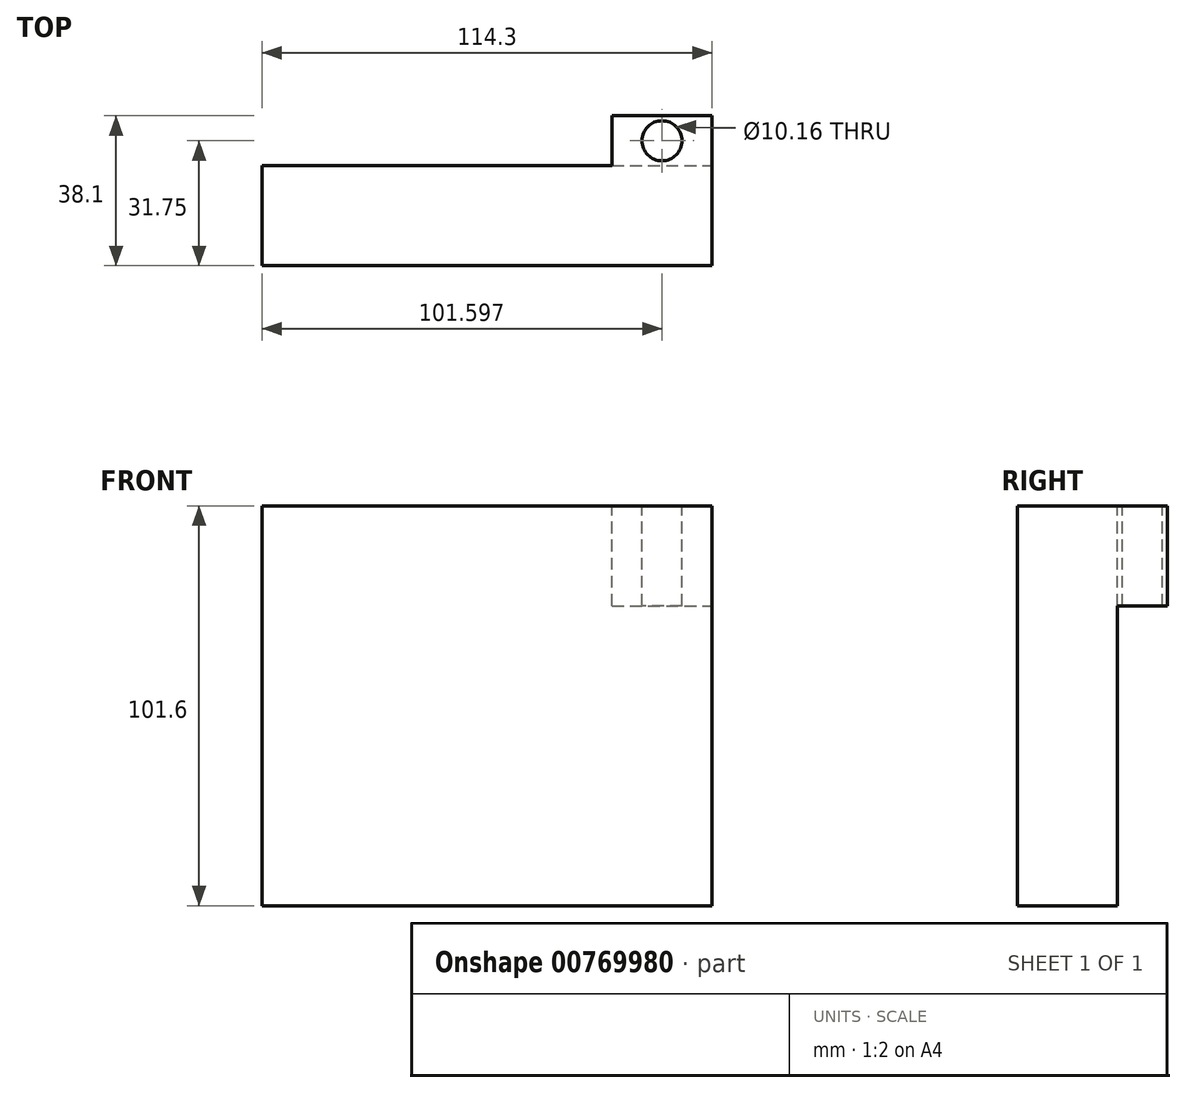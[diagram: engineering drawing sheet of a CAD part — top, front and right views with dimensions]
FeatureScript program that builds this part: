
annotation { "Feature Type Name" : "Feature", "Feature Type Description" : "" }
export const myFeature = defineFeature(function(context is Context, id is Id, definition is map)
    precondition{}
    {
        {
            var Q0;
            Q0=qCreatedBy(makeId("Front.planeOp"),FACE);
            var sketch = newSketch(context, id + "F0", { "sketchPlane" : qUnion([Q0])});
            skLineSegment(sketch, "E0.bottom", {"start": v(-101.4, 95.41) * mm, "end": v(12.9, 95.41) * mm});
            skLineSegment(sketch, "E0.top", {"start": v(-101.4, -6.19) * mm, "end": v(12.9, -6.19) * mm});
            skLineSegment(sketch, "E0.left", {"start": v(-101.4, 95.41) * mm, "end": v(-101.4, -6.19) * mm});
            skLineSegment(sketch, "E0.right", {"start": v(12.9, 95.41) * mm, "end": v(12.9, -6.19) * mm});
            skSolve(sketch);
        }
        {
            var Q0;
            Q0 = qSketchRegion(id + "F0", true);
            extrude(context, id + "F1", {"entities" : qUnion([Q0]), "depth" : 25.4 * mm, "offsetDistance" : 25.4 * mm});
        }
        {
            var Q0;
            {var subQ0=sQuery(id+"F0.wireOp",EDGE,"E0.bottom");Q0=makeQuery(id+"FLVJZS1soLFqfxB_1.boolean.opBoolean","MERGE",FACE,{"derivedFrom":[makeQuery(id+"F2oU1E1NIX52K6T_1.boolean.opBoolean","MERGE",FACE,{"derivedFrom":[makeQuery(id+"F1.opExtrude","SWEPT_FACE",FACE,{"disambiguationData":[OSD([subQ0])]}),makeQuery(id+"F2oU1E1NIX52K6T_1.opExtrude","SWEPT_FACE",FACE,{"disambiguationData":[OSD([subQ0,sQuery(id+"F0.wireOp",EDGE,"E0.left")])]})]}),makeQuery(id+"FLVJZS1soLFqfxB_1.opExtrude","SWEPT_FACE",FACE,{"disambiguationData":[OSD([subQ0,sQuery(id+"F0.wireOp",EDGE,"E0.right")])]})]});}
            var sketch = newSketch(context, id + "F2", { "sketchPlane" : qUnion([Q0])});
            skLineSegment(sketch, "E1.bottom", {"start": v(-12.5, 0) * mm, "end": v(12.9, 0) * mm});
            skLineSegment(sketch, "E1.top", {"start": v(-12.5, 12.7) * mm, "end": v(12.9, 12.7) * mm});
            skLineSegment(sketch, "E1.left", {"start": v(-12.5, 0) * mm, "end": v(-12.5, 12.7) * mm});
            skLineSegment(sketch, "E1.right", {"start": v(12.9, 0) * mm, "end": v(12.9, 12.7) * mm});
            skPoint(sketch, "E2", {"position": v(-44.24, 6.35) * mm});
            skPoint(sketch, "E2.positionSnap0", {"position": v(-44.24, 0) * mm});
            skPoint(sketch, "E2.positionSnap1", {"position": v(12.9, 6.35) * mm});
            skSolve(sketch);
        }
        {
            var Q0;
            Q0=makeQuery(id+"F2.imprint","IMPRINT",FACE,{"disambiguationData":[TD([[makeQuery(id+"F2.imprint","IMPRINT",EDGE,{"derivedFrom":sQuery(id+"F2.wireOp",EDGE,"E1.bottom")}),1.0]])]});
            extrude(context, id + "F3", {"entities" : qUnion([Q0]), "oppositeDirection" : true, "depth" : 25.4 * mm, "offsetDistance" : 25.4 * mm});
        }
        {
            var Q0;
            Q0=sQuery(id+"F2.wireOp",VERTEX,"E2");
            var Q1;
            Q1=makeQuery(id+"F3.opExtrude","SWEPT_BODY",BODY,{"disambiguationData":[OSD([sQuery(id+"F2.wireOp",EDGE,"E1.bottom"),sQuery(id+"F2.wireOp",EDGE,"E1.top"),sQuery(id+"F2.wireOp",EDGE,"E1.left"),sQuery(id+"F2.wireOp",EDGE,"E1.right")])]});
            hole(context, id + "F4", {"style" : HoleStyle.SIMPLE, "endStyle" : HoleEndStyle.THROUGH, "holeDiameter" : 10.16 * mm, "majorDiameter" : 6.35 * mm, "isTappedThrough" : true, "tappedDepth" : 12.7 * mm, "tapClearance" : 3, "locations" : qUnion([Q0]), "scope" : qUnion([Q1])});
        }
        {
            var Q0;
            Q0=makeQuery(id+"F3.opExtrude","SWEPT_BODY",BODY,{"disambiguationData":[OSD([sQuery(id+"F2.wireOp",EDGE,"E1.bottom"),sQuery(id+"F2.wireOp",EDGE,"E1.top"),sQuery(id+"F2.wireOp",EDGE,"E1.left"),sQuery(id+"F2.wireOp",EDGE,"E1.right")])]});
            var Q1;
            Q1=makeQuery(id+"F1.opExtrude","SWEPT_BODY",BODY,{"disambiguationData":[OSD([sQuery(id+"F0.wireOp",EDGE,"E0.bottom"),sQuery(id+"F0.wireOp",EDGE,"E0.top"),sQuery(id+"F0.wireOp",EDGE,"E0.left"),sQuery(id+"F0.wireOp",EDGE,"E0.right")])]});
            booleanBodies(context, id + "F5", {"operationType" : BooleanOperationType.UNION, "tools" : qUnion([Q0, Q1])});
        }
        {
            var Q0;
            Q0=makeQuery(id+"F5.opBoolean","MERGE",FACE,{"derivedFrom":[makeQuery(id+"F1.opExtrude","SWEPT_FACE",FACE,{"disambiguationData":[OSD([sQuery(id+"F0.wireOp",EDGE,"E0.bottom")])]}),makeQuery(id+"F3.opExtrude","CAP_FACE",FACE,{"disambiguationData":[OSD([sQuery(id+"F2.wireOp",EDGE,"E1.bottom"),sQuery(id+"F2.wireOp",EDGE,"E1.top"),sQuery(id+"F2.wireOp",EDGE,"E1.left"),sQuery(id+"F2.wireOp",EDGE,"E1.right")])],"isStart":true})]});
            var sketch = newSketch(context, id + "F6", { "sketchPlane" : qUnion([Q0])});
            skPoint(sketch, "E3", {"position": v(0.2, 6.35) * mm});
            skSolve(sketch);
        }
        {
            var Q0;
            Q0=sQuery(id+"F6.wireOp",VERTEX,"E3");
            var Q1;
            Q1=makeQuery(id+"F3.opExtrude","SWEPT_BODY",BODY,{"disambiguationData":[OSD([sQuery(id+"F2.wireOp",EDGE,"E1.bottom"),sQuery(id+"F2.wireOp",EDGE,"E1.top"),sQuery(id+"F2.wireOp",EDGE,"E1.left"),sQuery(id+"F2.wireOp",EDGE,"E1.right")])]});
            hole(context, id + "F7", {"style" : HoleStyle.SIMPLE, "endStyle" : HoleEndStyle.THROUGH, "holeDiameter" : 10.16 * mm, "majorDiameter" : 6.35 * mm, "isTappedThrough" : true, "tappedDepth" : 12.7 * mm, "tapClearance" : 3, "locations" : qUnion([Q0]), "scope" : qUnion([Q1])});
        }
    });
